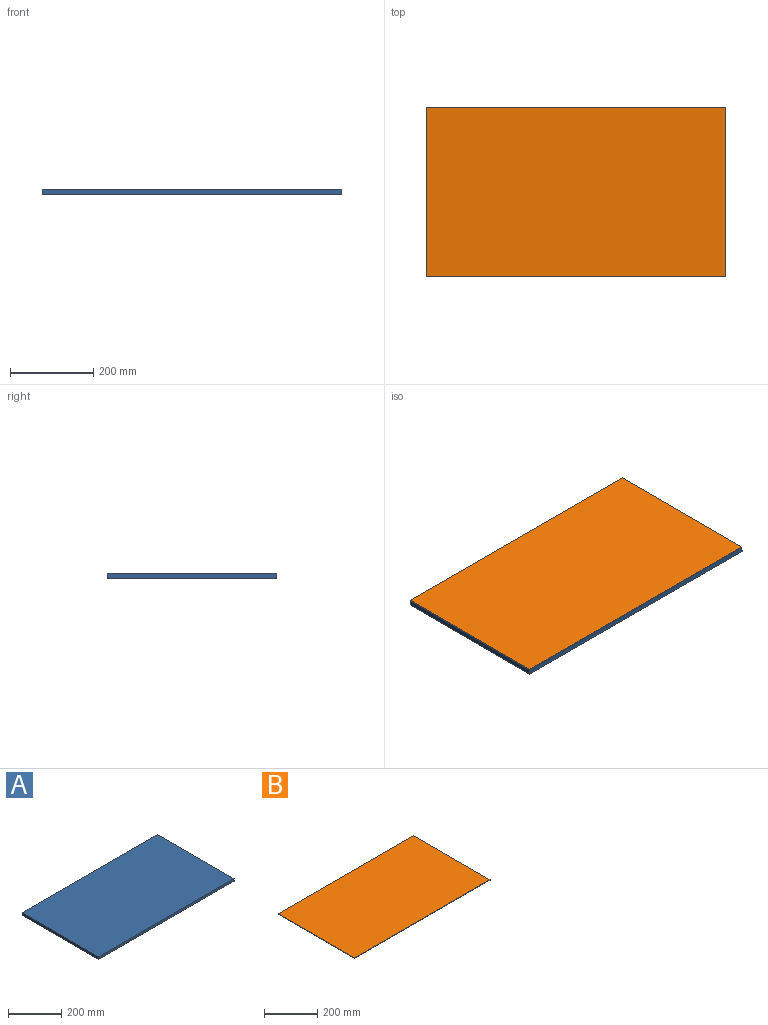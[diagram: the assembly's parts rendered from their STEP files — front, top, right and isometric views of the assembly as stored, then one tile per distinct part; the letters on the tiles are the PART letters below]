
ASSEMBLY  parts=2 mates=1
PART A: 6 faces, bbox 720x407x12 mm
  f0: plane 720x12mm, normal (0,1,0), area 8640mm2, adj f1,f3,f4,f5
  f1: plane 720x407mm, normal (0,0,1), area 293040mm2, adj f0,f2,f4,f5
  f2: plane 720x12mm, normal (0,-1,0), area 8640mm2, adj f1,f3,f4,f5
  f3: plane 720x407mm, normal (0,0,-1), area 293040mm2, adj f0,f2,f4,f5
  f4: plane 407x12mm, normal (1,0,0), area 4884mm2, adj f0,f1,f2,f3
  f5: plane 407x12mm, normal (-1,0,0), area 4884mm2, adj f0,f1,f2,f3
PART B: 6 faces, bbox 720x407x2 mm
  f0: plane 720x407mm, normal (0,0,1), area 293040mm2, adj f1,f3,f4,f5
  f1: plane 720x2mm, normal (0,-1,0), area 1440mm2, adj f0,f2,f4,f5
  f2: plane 720x407mm, normal (0,0,-1), area 293040mm2, adj f1,f3,f4,f5
  f3: plane 720x2mm, normal (0,1,0), area 1440mm2, adj f0,f2,f4,f5
  f4: plane 407x2mm, normal (1,0,0), area 814mm2, adj f0,f1,f2,f3
  f5: plane 407x2mm, normal (-1,0,0), area 814mm2, adj f0,f1,f2,f3
PLACE A t=(-58.5,156.79,-51.13)mm
PLACE B t=(-58.5,156.79,-51.13)mm
MATE fastened A.f1 <-> B.f2  axis (0,0,1) through (-58.5,60.94,-153.69)mm
